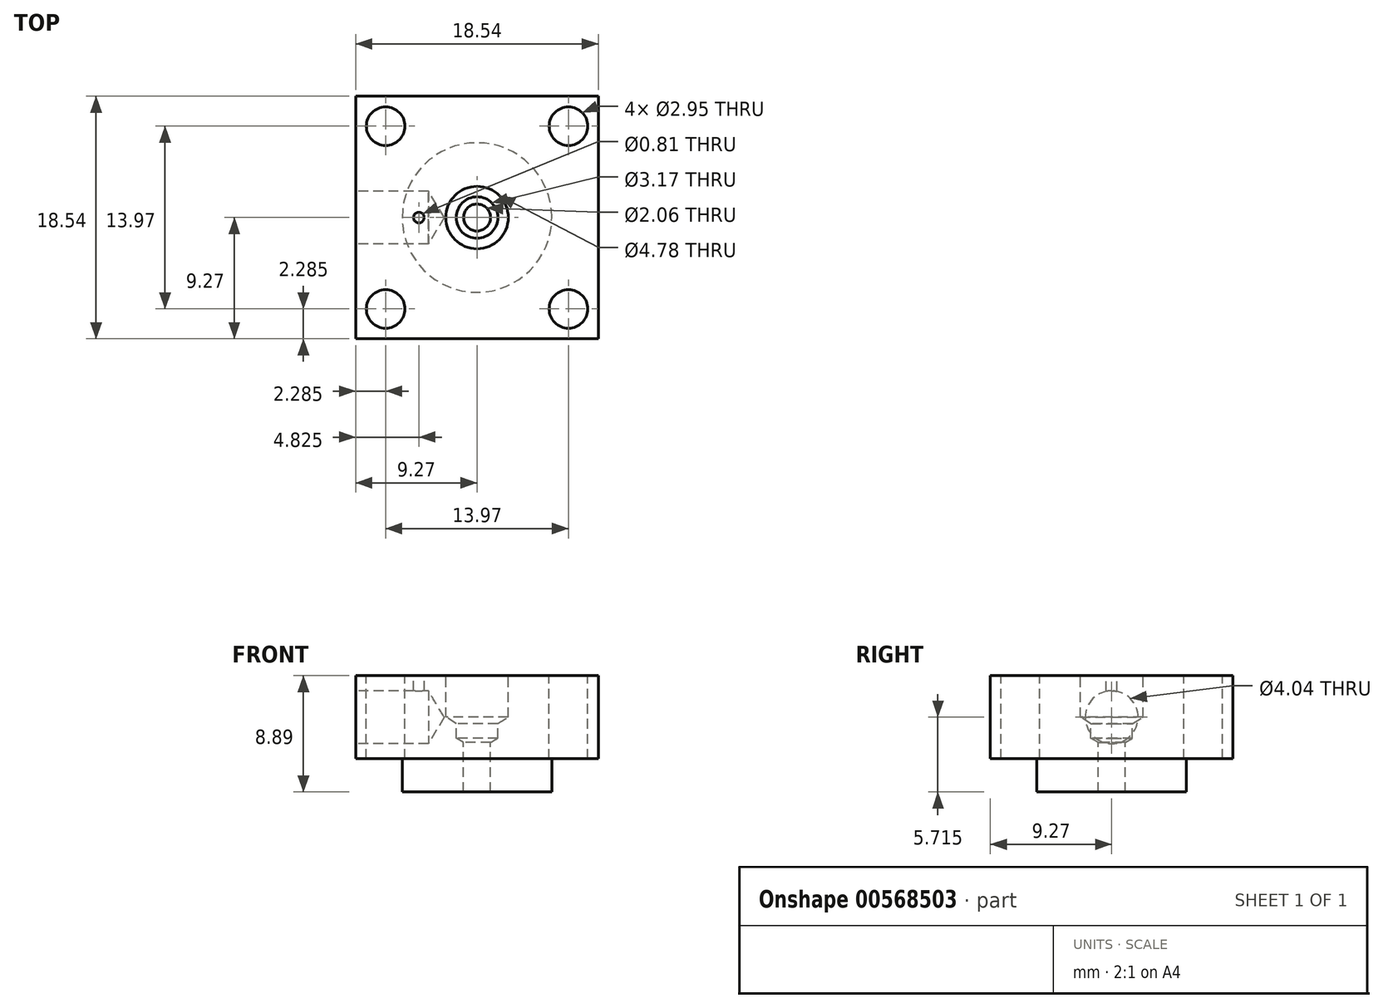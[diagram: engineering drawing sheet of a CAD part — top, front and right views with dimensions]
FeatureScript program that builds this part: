
annotation { "Feature Type Name" : "Feature", "Feature Type Description" : "" }
export const myFeature = defineFeature(function(context is Context, id is Id, definition is map)
    precondition{}
    {
        {
            var Q0;
            Q0=qCreatedBy(makeId("Top.planeOp"),FACE);
            var sketch = newSketch(context, id + "F0", { "sketchPlane" : qUnion([Q0])});
            skLineSegment(sketch, "E0.bottom", {"start": v(-9.27, 9.27) * mm, "end": v(9.27, 9.27) * mm});
            skLineSegment(sketch, "E0.top", {"start": v(-9.27, -9.27) * mm, "end": v(9.27, -9.27) * mm});
            skLineSegment(sketch, "E0.left", {"start": v(-9.27, 9.27) * mm, "end": v(-9.27, -9.27) * mm});
            skLineSegment(sketch, "E0.right", {"start": v(9.27, 9.27) * mm, "end": v(9.27, -9.27) * mm});
            skPoint(sketch, "E0.middle", {"position": v(0, 0) * mm});
            skSolve(sketch);
        }
        {
            var Q0;
            Q0 = qSketchRegion(id + "F0", true);
            extrude(context, id + "F1", {"entities" : qUnion([Q0]), "depth" : 8.9 * mm, "offsetDistance" : 25.4 * mm});
        }
        {
            var Q0;
            Q0=makeQuery(id+"F1.opExtrude","CAP_FACE",FACE,{"disambiguationData":[OSD([sQuery(id+"F0.wireOp",EDGE,"E0.bottom"),sQuery(id+"F0.wireOp",EDGE,"E0.top"),sQuery(id+"F0.wireOp",EDGE,"E0.left"),sQuery(id+"F0.wireOp",EDGE,"E0.right")])],"isStart":false});
            var sketch = newSketch(context, id + "F2", { "sketchPlane" : qUnion([Q0])});
            skCircle(sketch, "E1", {"center": v(0, 0) * mm, "radius": 1.03 * mm});
            skSolve(sketch);
        }
        {
            var Q0;
            Q0 = qSketchRegion(id + "F2", true);
            extrude(context, id + "F3", {"entities" : qUnion([Q0]), "operationType" : NewBodyOperationType.REMOVE, "endBound" : BoundingType.THROUGH_ALL, "oppositeDirection" : true, "depth" : 25.4 * mm, "offsetDistance" : 25.4 * mm});
        }
        {
            var Q0;
            Q0=makeQuery(id+"F1.opExtrude","CAP_FACE",FACE,{"disambiguationData":[OSD([sQuery(id+"F0.wireOp",EDGE,"E0.bottom"),sQuery(id+"F0.wireOp",EDGE,"E0.top"),sQuery(id+"F0.wireOp",EDGE,"E0.left"),sQuery(id+"F0.wireOp",EDGE,"E0.right")])],"isStart":false});
            var sketch = newSketch(context, id + "F4", { "sketchPlane" : qUnion([Q0])});
            skPoint(sketch, "E2", {"position": v(0, 0) * mm});
            skSolve(sketch);
        }
        {
            var Q0;
            Q0=sQuery(id+"F4.wireOp",VERTEX,"E2");
            var Q1;
            Q1=makeQuery(id+"F1.opExtrude","SWEPT_BODY",BODY,{"disambiguationData":[OSD([sQuery(id+"F0.wireOp",EDGE,"E0.bottom"),sQuery(id+"F0.wireOp",EDGE,"E0.top"),sQuery(id+"F0.wireOp",EDGE,"E0.left"),sQuery(id+"F0.wireOp",EDGE,"E0.right")])]});
            hole(context, id + "F5", {"style" : HoleStyle.SIMPLE, "endStyle" : HoleEndStyle.BLIND, "holeDiameter" : 3.17 * mm, "holeDepth" : 4.78 * mm, "isTappedThrough" : true, "tappedDepth" : 8.9 * mm, "tapClearance" : 3, "locations" : qUnion([Q0]), "scope" : qUnion([Q1])});
        }
        {
            var Q0;
            Q0=makeQuery(id+"F1.opExtrude","CAP_FACE",FACE,{"disambiguationData":[OSD([sQuery(id+"F0.wireOp",EDGE,"E0.bottom"),sQuery(id+"F0.wireOp",EDGE,"E0.top"),sQuery(id+"F0.wireOp",EDGE,"E0.left"),sQuery(id+"F0.wireOp",EDGE,"E0.right")])],"isStart":false});
            var sketch = newSketch(context, id + "F6", { "sketchPlane" : qUnion([Q0])});
            skPoint(sketch, "E3", {"position": v(0, 0) * mm});
            skSolve(sketch);
        }
        {
            var Q0;
            Q0=sQuery(id+"F6.wireOp",VERTEX,"E3");
            var Q1;
            Q1=makeQuery(id+"F1.opExtrude","SWEPT_BODY",BODY,{"disambiguationData":[OSD([sQuery(id+"F0.wireOp",EDGE,"E0.bottom"),sQuery(id+"F0.wireOp",EDGE,"E0.top"),sQuery(id+"F0.wireOp",EDGE,"E0.left"),sQuery(id+"F0.wireOp",EDGE,"E0.right")])]});
            hole(context, id + "F7", {"style" : HoleStyle.SIMPLE, "endStyle" : HoleEndStyle.BLIND, "holeDiameter" : 4.78 * mm, "holeDepth" : 3.17 * mm, "isTappedThrough" : true, "tappedDepth" : 8.9 * mm, "tapClearance" : 3, "locations" : qUnion([Q0]), "scope" : qUnion([Q1])});
        }
        {
            var Q0;
            Q0=makeQuery(id+"F1.opExtrude","CAP_FACE",FACE,{"disambiguationData":[OSD([sQuery(id+"F0.wireOp",EDGE,"E0.bottom"),sQuery(id+"F0.wireOp",EDGE,"E0.top"),sQuery(id+"F0.wireOp",EDGE,"E0.left"),sQuery(id+"F0.wireOp",EDGE,"E0.right")])],"isStart":false});
            var sketch = newSketch(context, id + "F8", { "sketchPlane" : qUnion([Q0])});
            skCircle(sketch, "E4", {"center": v(-4.45, 0) * mm, "radius": 0.4 * mm});
            skSolve(sketch);
        }
        {
            var Q0;
            Q0 = qSketchRegion(id + "F8", true);
            extrude(context, id + "F9", {"entities" : qUnion([Q0]), "operationType" : NewBodyOperationType.REMOVE, "oppositeDirection" : true, "depth" : 3.17 * mm, "offsetDistance" : 25.4 * mm});
        }
        {
            var Q0;
            Q0=makeQuery(id+"F1.opExtrude","CAP_FACE",FACE,{"disambiguationData":[OSD([sQuery(id+"F0.wireOp",EDGE,"E0.bottom"),sQuery(id+"F0.wireOp",EDGE,"E0.top"),sQuery(id+"F0.wireOp",EDGE,"E0.left"),sQuery(id+"F0.wireOp",EDGE,"E0.right")])],"isStart":false});
            var sketch = newSketch(context, id + "F10", { "sketchPlane" : qUnion([Q0])});
            skCircle(sketch, "E5", {"center": v(-6.99, 6.99) * mm, "radius": 1.47 * mm});
            skCircle(sketch, "E6.0.1.0", {"center": v(-6.99, -6.99) * mm, "radius": 1.47 * mm});
            skCircle(sketch, "E6.1.0.0", {"center": v(6.99, 6.99) * mm, "radius": 1.47 * mm});
            skCircle(sketch, "E6.1.1.0", {"center": v(6.99, -6.99) * mm, "radius": 1.47 * mm});
            skLineSegment(sketch, "E6.direction1", {"start": v(-6.99, 6.99) * mm, "end": v(6.99, 6.99) * mm, "construction": true});
            skLineSegment(sketch, "E6.direction2", {"start": v(-6.99, 6.99) * mm, "end": v(-6.99, -6.99) * mm, "construction": true});
            skSolve(sketch);
        }
        {
            var Q0;
            Q0 = qSketchRegion(id + "F10", true);
            extrude(context, id + "F11", {"entities" : qUnion([Q0]), "operationType" : NewBodyOperationType.REMOVE, "endBound" : BoundingType.THROUGH_ALL, "oppositeDirection" : true, "depth" : 25.4 * mm, "offsetDistance" : 25.4 * mm});
        }
        {
            var Q0;
            Q0=makeQuery(id+"F1.opExtrude","CAP_FACE",FACE,{"disambiguationData":[OSD([sQuery(id+"F0.wireOp",EDGE,"E0.bottom"),sQuery(id+"F0.wireOp",EDGE,"E0.top"),sQuery(id+"F0.wireOp",EDGE,"E0.left"),sQuery(id+"F0.wireOp",EDGE,"E0.right")])],"isStart":true});
            var sketch = newSketch(context, id + "F12", { "sketchPlane" : qUnion([Q0])});
            skCircle(sketch, "E7", {"center": v(0, 0) * mm, "radius": 5.72 * mm});
            skLineSegment(sketch, "E8.bottom", {"start": v(-9.27, 9.27) * mm, "end": v(9.27, 9.27) * mm});
            skLineSegment(sketch, "E8.top", {"start": v(-9.27, -9.27) * mm, "end": v(9.27, -9.27) * mm});
            skLineSegment(sketch, "E8.left", {"start": v(-9.27, 9.27) * mm, "end": v(-9.27, -9.27) * mm});
            skLineSegment(sketch, "E8.right", {"start": v(9.27, 9.27) * mm, "end": v(9.27, -9.27) * mm});
            skSolve(sketch);
        }
        {
            var Q0;
            Q0 = qSketchRegion(id + "F12", true);
            extrude(context, id + "F13", {"entities" : qUnion([Q0]), "operationType" : NewBodyOperationType.REMOVE, "oppositeDirection" : true, "depth" : 2.54 * mm, "offsetDistance" : 25.4 * mm});
        }
        {
            var Q0;
            Q0=makeQuery(id+"F1.opExtrude","SWEPT_FACE",FACE,{"disambiguationData":[OSD([sQuery(id+"F0.wireOp",EDGE,"E0.left")])]});
            var sketch = newSketch(context, id + "F14", { "sketchPlane" : qUnion([Q0])});
            skCircle(sketch, "E9", {"center": v(0, 5.71) * mm, "radius": 2.02 * mm});
            skSolve(sketch);
        }
        {
            var Q0;
            Q0=sQuery(id+"F14.wireOp",VERTEX,"E9.center");
            var Q1;
            Q1=makeQuery(id+"F1.opExtrude","SWEPT_BODY",BODY,{"disambiguationData":[OSD([sQuery(id+"F0.wireOp",EDGE,"E0.bottom"),sQuery(id+"F0.wireOp",EDGE,"E0.top"),sQuery(id+"F0.wireOp",EDGE,"E0.left"),sQuery(id+"F0.wireOp",EDGE,"E0.right")])]});
            hole(context, id + "F15", {"style" : HoleStyle.SIMPLE, "endStyle" : HoleEndStyle.BLIND, "holeDiameter" : 4.04 * mm, "holeDepth" : 5.56 * mm, "isTappedThrough" : true, "tappedDepth" : 8.9 * mm, "tapClearance" : 3, "locations" : qUnion([Q0]), "scope" : qUnion([Q1])});
        }
    });
